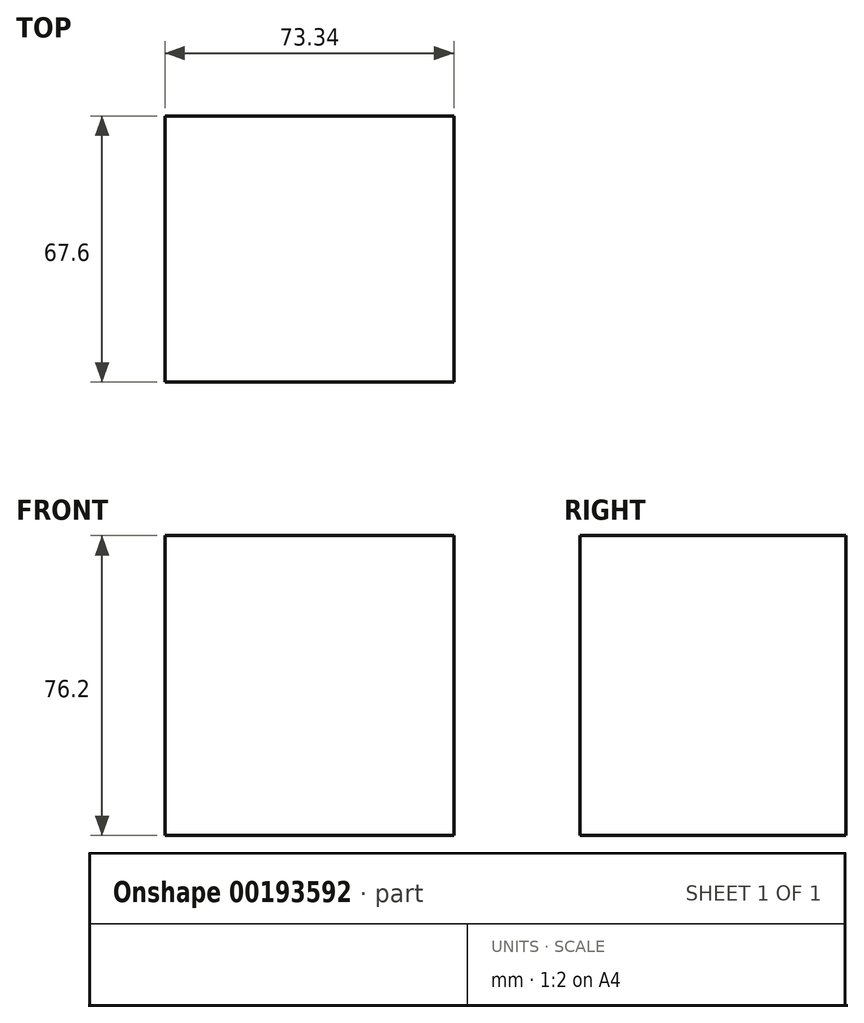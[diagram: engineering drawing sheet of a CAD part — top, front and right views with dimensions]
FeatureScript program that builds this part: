
annotation { "Feature Type Name" : "Feature", "Feature Type Description" : "" }
export const myFeature = defineFeature(function(context is Context, id is Id, definition is map)
    precondition{}
    {
        {
            var Q0;
            Q0=qCreatedBy(makeId("Top.planeOp"),FACE);
            var sketch = newSketch(context, id + "F0", { "sketchPlane" : qUnion([Q0])});
            skLineSegment(sketch, "E0.bottom", {"start": v(-36.67, 33.8) * mm, "end": v(36.67, 33.8) * mm});
            skLineSegment(sketch, "E0.top", {"start": v(-36.67, -33.8) * mm, "end": v(36.67, -33.8) * mm});
            skLineSegment(sketch, "E0.left", {"start": v(-36.67, 33.8) * mm, "end": v(-36.67, -33.8) * mm});
            skLineSegment(sketch, "E0.right", {"start": v(36.67, 33.8) * mm, "end": v(36.67, -33.8) * mm});
            skPoint(sketch, "E0.middle", {"position": v(0, 0) * mm});
            skSolve(sketch);
        }
        {
            var Q0;
            Q0 = qSketchRegion(id + "F0", true);
            extrude(context, id + "F1", {"entities" : qUnion([Q0]), "depth" : 76.2 * mm});
        }
    });
